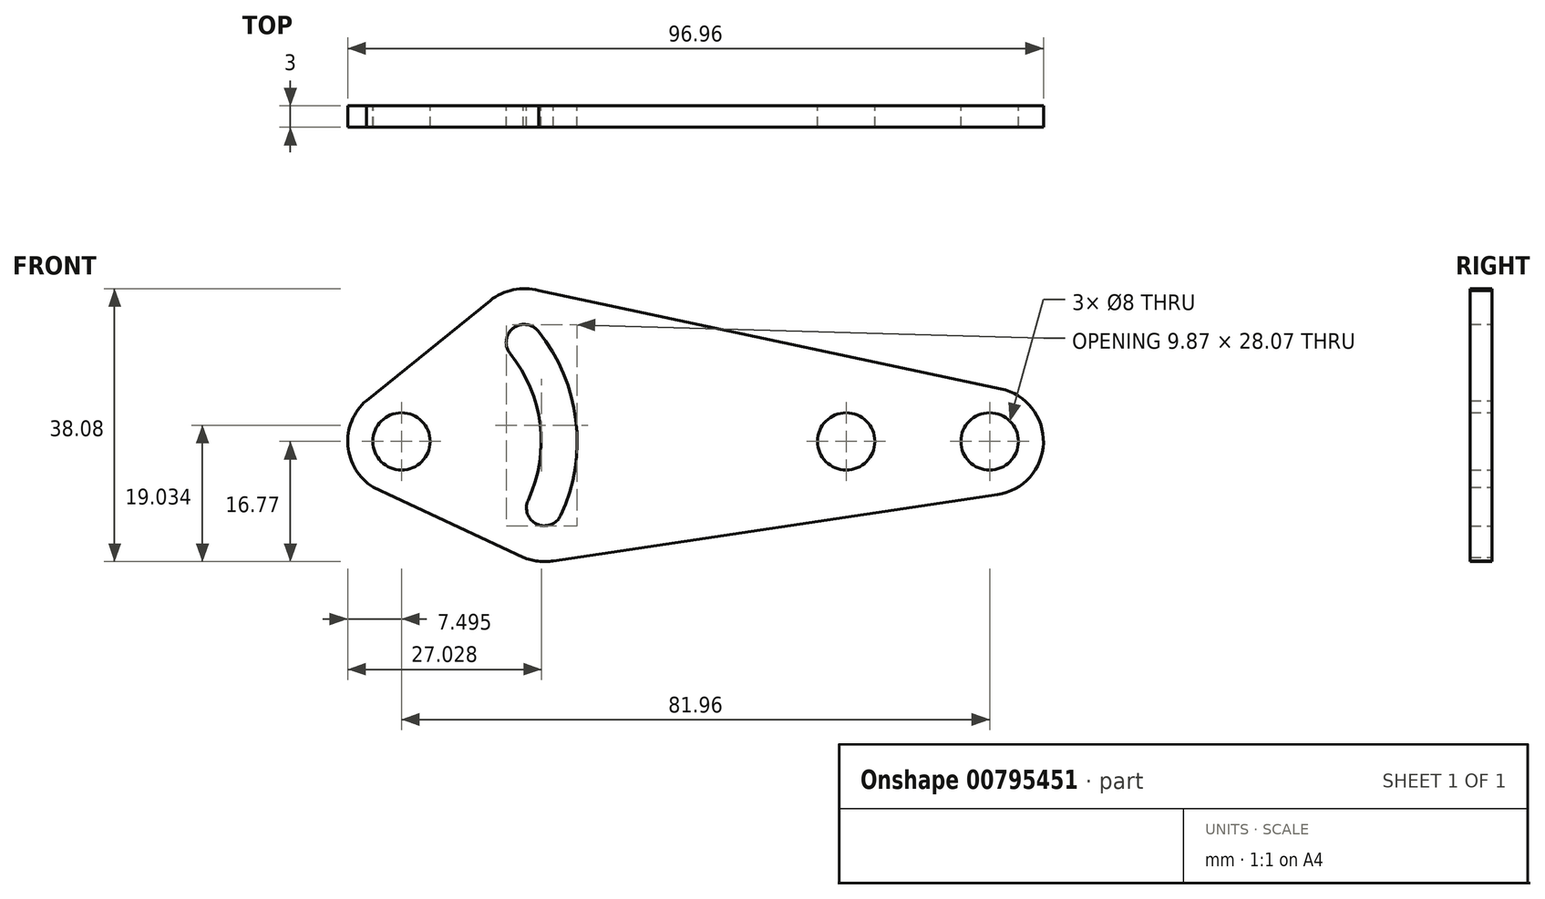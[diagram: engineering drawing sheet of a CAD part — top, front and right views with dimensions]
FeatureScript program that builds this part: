
annotation { "Feature Type Name" : "Feature", "Feature Type Description" : "" }
export const myFeature = defineFeature(function(context is Context, id is Id, definition is map)
    precondition{}
    {
        {
            var Q0;
            Q0=qCreatedBy(makeId("Front.planeOp"),FACE);
            var sketch = newSketch(context, id + "F0", { "sketchPlane" : qUnion([Q0])});
            skPoint(sketch, "E0.middle", {"position": v(0, 0) * mm});
            skCircle(sketch, "E1", {"center": v(-30.41, 0) * mm, "radius": 4 * mm});
            skPoint(sketch, "E2", {"position": v(49.03, 0) * mm});
            skArc(sketch, "E3", {"start": v(-11.38, 15.38) * mm, "mid": v(-14.9, 15.76) * mm, "end": v(-15.27, 12.24) * mm});
            skArc(sketch, "E4", {"start": v(-12.76, -8.22) * mm, "mid": v(-11.55, -11.54) * mm, "end": v(-8.23, -10.33) * mm});
            skArc(sketch, "E5", {"start": v(-11.27, 21.02) * mm, "mid": v(-14.82, 21.16) * mm, "end": v(-18.04, 19.64) * mm});
            skArc(sketch, "E6", {"start": v(-13.48, -16.15) * mm, "mid": v(-11.4, -16.72) * mm, "end": v(-9.23, -16.66) * mm});
            skArc(sketch, "E7", {"start": v(-35.31, 5.68) * mm, "mid": v(-37.9, -0.6) * mm, "end": v(-34.35, -6.39) * mm});
            skLineSegment(sketch, "E8", {"start": v(-35.31, 5.68) * mm, "end": v(-18.04, 19.64) * mm});
            skLineSegment(sketch, "E9", {"start": v(-13.48, -16.15) * mm, "end": v(-34.35, -6.39) * mm});
            skLineSegment(sketch, "E10", {"start": v(50.28, -16.04) * mm, "end": v(50.42, -16.04) * mm});
            skArc(sketch, "E11", {"start": v(-12.76, -8.22) * mm, "mid": v(-11.09, 2.37) * mm, "end": v(-15.27, 12.24) * mm});
            skArc(sketch, "E12", {"start": v(-8.23, -10.33) * mm, "mid": v(-6.13, 2.98) * mm, "end": v(-11.38, 15.38) * mm});
            skCircle(sketch, "E13", {"center": v(31.56, 0) * mm, "radius": 4 * mm});
            skLineSegment(sketch, "E14", {"start": v(59.02, 0) * mm, "end": v(51.55, 0) * mm});
            skCircle(sketch, "E15", {"center": v(51.55, 0) * mm, "radius": 4 * mm});
            skArc(sketch, "E16", {"start": v(52.65, -7.42) * mm, "mid": v(59.04, -0.23) * mm, "end": v(53.1, 7.34) * mm});
            skLineSegment(sketch, "E17", {"start": v(-11.27, 21.02) * mm, "end": v(53.1, 7.34) * mm});
            skLineSegment(sketch, "E18", {"start": v(-9.23, -16.66) * mm, "end": v(52.65, -7.42) * mm});
            skSolve(sketch);
        }
        {
            var Q0;
            Q0=makeQuery(id+"F0.imprint","IMPRINT",FACE,{"disambiguationData":[TD([[makeQuery(id+"F0.imprint","IMPRINT",EDGE,{"derivedFrom":sQuery(id+"F0.wireOp",EDGE,"E1")}),-1.0]])]});
            extrude(context, id + "F1", {"entities" : qUnion([Q0]), "depth" : 3 * mm, "offsetDistance" : 25 * mm});
        }
    });
